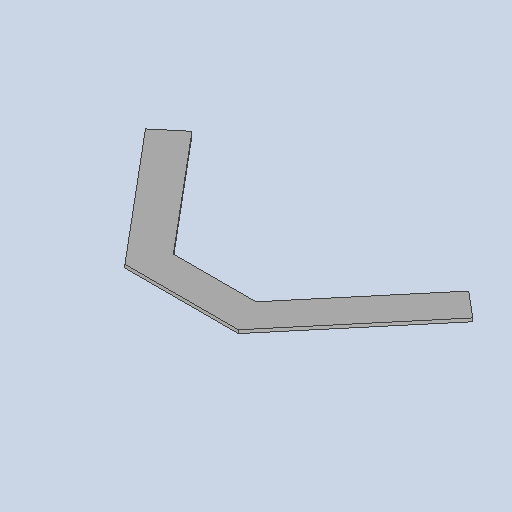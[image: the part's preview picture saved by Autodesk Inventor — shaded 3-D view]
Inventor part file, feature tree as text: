
AUTODESK INVENTOR PART (.ipt)
format: ipt  version: 2025 (Build 290162010, 162A)  size: 282,112 bytes
history: native  units: mm
features: other x2, sheet_metal_op x1, sketch x1
ambient origin geometry x8: Origin, YZ Plane, XZ Plane, XY Plane, X Axis, Y Axis, Z Axis, Center Point
bodies: Solid1 (feature_tree)
feature tree (4):
  sheet_metal_op  "Face1"
  sketch  "Sketch1"  dims[d0=50.0mm d1=70.0mm d2=22.68928mm d3=20.0mm d4=2.0mm]
  other  "Plate1"
  other  "Definition1"
